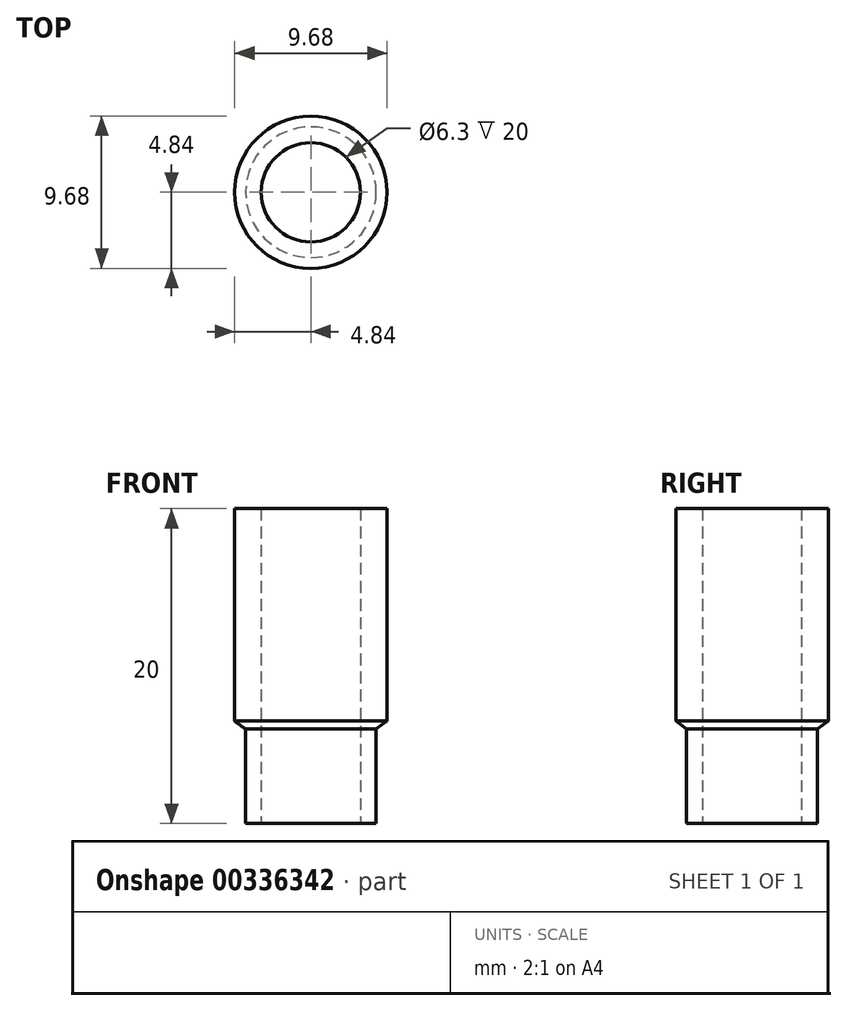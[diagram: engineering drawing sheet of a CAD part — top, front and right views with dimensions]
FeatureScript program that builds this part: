
annotation { "Feature Type Name" : "Feature", "Feature Type Description" : "" }
export const myFeature = defineFeature(function(context is Context, id is Id, definition is map)
    precondition{}
    {
        {
            var Q0;
            Q0=qCreatedBy(makeId("Top.planeOp"),FACE);
            var sketch = newSketch(context, id + "F0", { "sketchPlane" : qUnion([Q0])});
            skCircle(sketch, "E0", {"center": v(0, 0) * mm, "radius": 4.84 * mm});
            skCircle(sketch, "E1", {"center": v(0, 0) * mm, "radius": 3.15 * mm});
            skSolve(sketch);
        }
        {
            var Q0;
            Q0 = qSketchRegion(id + "F0", true);
            extrude(context, id + "F1", {"entities" : qUnion([Q0]), "depth" : 20 * mm});
        }
        {
            var Q0;
            Q0=qCreatedBy(makeId("Front.planeOp"),FACE);
            var sketch = newSketch(context, id + "F2", { "sketchPlane" : qUnion([Q0])});
            skLineSegment(sketch, "E2", {"start": v(4.15, 0) * mm, "end": v(4.15, 6) * mm});
            skLineSegment(sketch, "E3", {"start": v(4.85, 6.5) * mm, "end": v(4.85, 0) * mm});
            skLineSegment(sketch, "E4", {"start": v(4.85, 0) * mm, "end": v(4.15, 0) * mm});
            skLineSegment(sketch, "E5", {"start": v(4.15, 6) * mm, "end": v(4.85, 6.5) * mm});
            skLineSegment(sketch, "E6", {"start": v(0, 0) * mm, "end": v(0, 10.08) * mm});
            skSolve(sketch);
        }
        {
            var Q0;
            Q0=makeQuery(id+"F2.imprint","IMPRINT",FACE,{"disambiguationData":[TD([[makeQuery(id+"F2.imprint","IMPRINT",EDGE,{"derivedFrom":sQuery(id+"F2.wireOp",EDGE,"E2")}),-1.0]])]});
            var Q1;
            Q1=sQuery(id+"F2.wireOp",EDGE,"E6");
            revolve(context, id + "F3", {"entities" : qUnion([Q0]), "axis" : qUnion([Q1]), "revolveType" : RevolveType.FULL});
        }
        {
            var Q0;
            Q0=makeQuery(id+"F3.opRevolve","SWEPT_BODY",BODY,{"disambiguationData":[OSD([sQuery(id+"F2.wireOp",EDGE,"E2"),sQuery(id+"F2.wireOp",EDGE,"E3"),sQuery(id+"F2.wireOp",EDGE,"E4"),sQuery(id+"F2.wireOp",EDGE,"E5")])]});
            var Q1;
            Q1=makeQuery(id+"F1.opExtrude","SWEPT_BODY",BODY,{"disambiguationData":[OSD([sQuery(id+"F0.wireOp",EDGE,"E0"),sQuery(id+"F0.wireOp",EDGE,"E1")])]});
            booleanBodies(context, id + "F4", {"operationType" : BooleanOperationType.SUBTRACTION, "tools" : qUnion([Q0]), "targets" : qUnion([Q1])});
        }
    });
